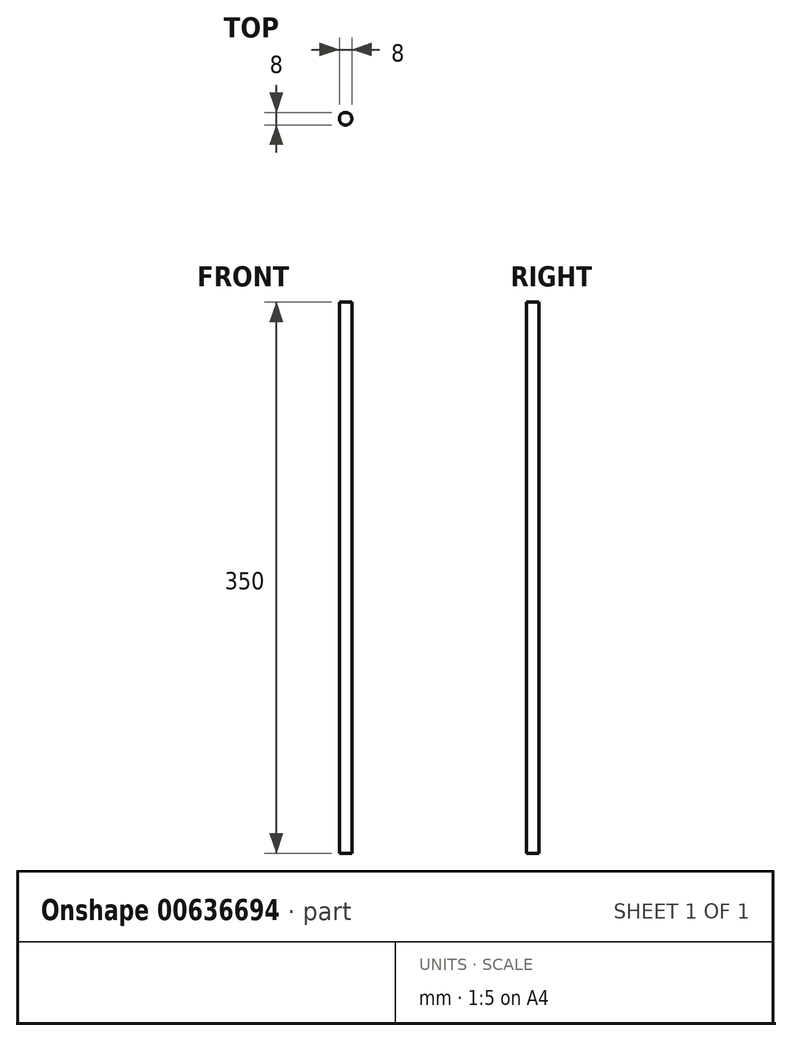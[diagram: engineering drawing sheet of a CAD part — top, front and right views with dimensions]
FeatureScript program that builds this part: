
annotation { "Feature Type Name" : "Feature", "Feature Type Description" : "" }
export const myFeature = defineFeature(function(context is Context, id is Id, definition is map)
    precondition{}
    {
        {
            assignVariable(context, id + "F0", {"name" : "h", "anyValue" : 350});
        }
        {
            var Q0;
            Q0=qCreatedBy(makeId("Top.planeOp"),FACE);
            var sketch = newSketch(context, id + "F1", { "sketchPlane" : qUnion([Q0])});
            skCircle(sketch, "E0", {"center": v(0, 0) * mm, "radius": 4 * mm});
            skSolve(sketch);
        }
        {
            var Q0;
            Q0 = qSketchRegion(id + "F1", true);
            extrude(context, id + "F2", {"entities" : qUnion([Q0]), "depth" : (getVariable(context, 'h')) * mm, "offsetDistance" : 25 * mm});
        }
    });
